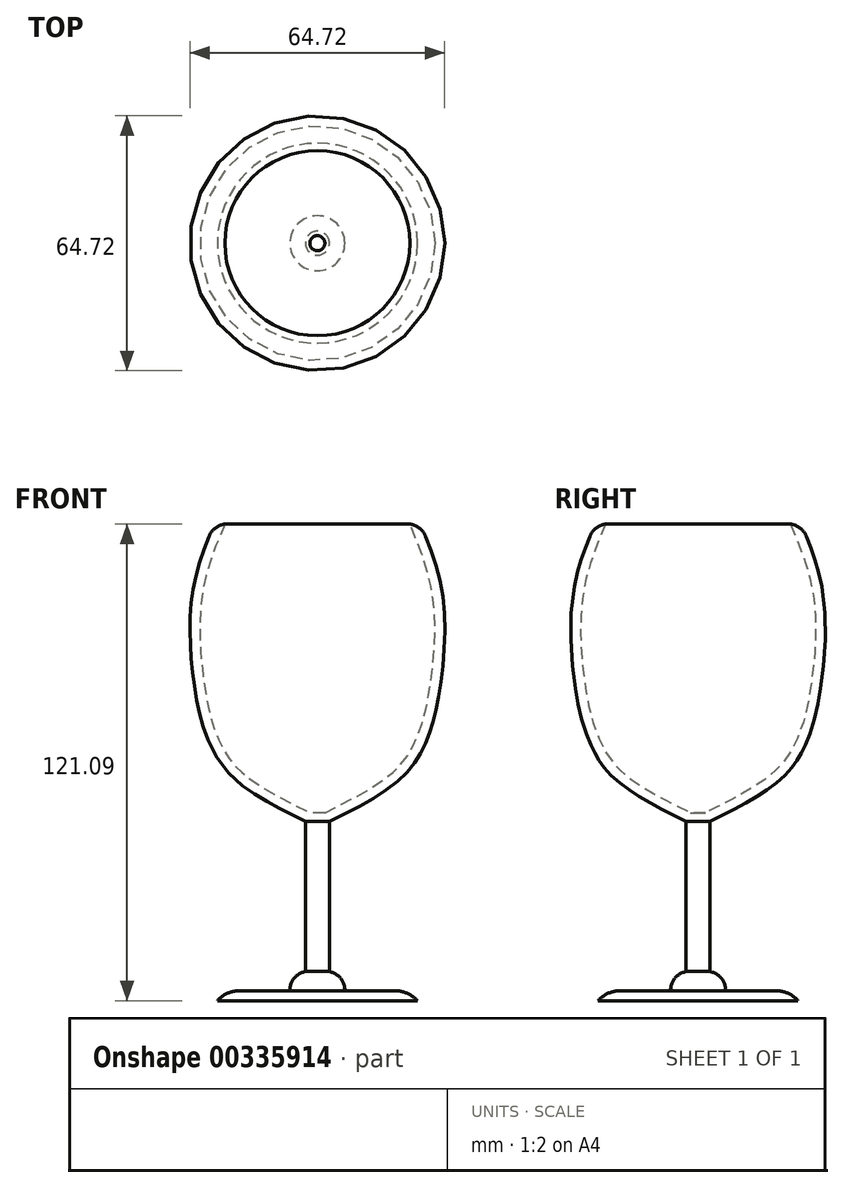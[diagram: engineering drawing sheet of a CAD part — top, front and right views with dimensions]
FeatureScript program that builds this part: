
annotation { "Feature Type Name" : "Feature", "Feature Type Description" : "" }
export const myFeature = defineFeature(function(context is Context, id is Id, definition is map)
    precondition{}
    {
        {
            var Q0;
            Q0=qCreatedBy(makeId("Front.planeOp"),FACE);
            var sketch = newSketch(context, id + "F0", { "sketchPlane" : qUnion([Q0])});
            skLineSegment(sketch, "E0", {"start": v(0, 0) * mm, "end": v(25.4, 0) * mm});
            skLineSegment(sketch, "E1", {"start": v(25.4, 0) * mm, "end": v(25.4, 2.54) * mm});
            skLineSegment(sketch, "E2", {"start": v(25.4, 2.54) * mm, "end": v(6.99, 2.54) * mm});
            skLineSegment(sketch, "E3", {"start": v(6.99, 2.54) * mm, "end": v(6.99, 7.38) * mm});
            skLineSegment(sketch, "E4", {"start": v(6.99, 7.38) * mm, "end": v(3.05, 7.38) * mm});
            skLineSegment(sketch, "E5", {"start": v(3.05, 7.38) * mm, "end": v(3.05, 45.48) * mm});
            skFitSpline(sketch, "E6", {"points": [v(3.05, 45.48) * mm, v(21.02, 56.27) * mm, v(27.66, 65.93) * mm, v(30.98, 78.3) * mm, v(31.88, 102.45) * mm, v(25.85, 122.06) * mm], "startDerivative": vector(93.63, 47.05) * mm, "endDerivative": vector(-35.34, 85.66) * mm});
            skFitSpline(sketch, "E7.0", {"points": [v(1.91, 47.75) * mm, v(3.86, 48.73) * mm, v(7.74, 50.68) * mm, v(12.23, 53.14) * mm, v(15.42, 55.15) * mm, v(17.21, 56.41) * mm, v(18.5, 57.44) * mm, v(19.38, 58.2) * mm, v(20.2, 58.98) * mm, v(21.18, 60.03) * mm, v(22.28, 61.37) * mm, v(23.4, 63.04) * mm, v(24.35, 64.77) * mm, v(25.05, 66.27) * mm, v(25.57, 67.51) * mm, v(26.05, 68.76) * mm, v(26.82, 71) * mm, v(27.56, 73.81) * mm, v(28.12, 76.63) * mm, v(28.42, 78.37) * mm, v(28.71, 80.2) * mm, v(29.05, 82.62) * mm, v(29.51, 86.74) * mm, v(29.8, 91.1) * mm, v(29.84, 95.48) * mm, v(29.72, 98.7) * mm, v(29.48, 101.3) * mm, v(29.2, 103.3) * mm, v(28.86, 105.25) * mm, v(28.33, 107.63) * mm, v(27.29, 111.32) * mm, v(25.7, 115.78) * mm, v(24.24, 119.3) * mm, v(23.5, 121.1) * mm]});
            skLineSegment(sketch, "E8", {"start": v(23.5, 121.1) * mm, "end": v(25.85, 122.06) * mm});
            skLineSegment(sketch, "E9", {"start": v(1.91, 47.75) * mm, "end": v(0, 47.75) * mm});
            skLineSegment(sketch, "E10", {"start": v(0, 47.75) * mm, "end": v(0, 0) * mm});
            skSolve(sketch);
        }
        {
            var Q0;
            Q0=makeQuery(id+"F0.imprint","IMPRINT",FACE,{"disambiguationData":[TD([[makeQuery(id+"F0.imprint","IMPRINT",EDGE,{"derivedFrom":sQuery(id+"F0.wireOp",EDGE,"E0")}),1.0]])]});
            var Q1;
            Q1=sQuery(id+"F0.wireOp",EDGE,"E10");
            revolve(context, id + "F1", {"entities" : qUnion([Q0]), "axis" : qUnion([Q1]), "revolveType" : RevolveType.FULL});
        }
        {
            var Q0;
            Q0=makeQuery(id+"F1.opRevolve","SWEPT_EDGE",EDGE,{"disambiguationData":[OSD([sQuery(id+"F0.wireOp",EDGE,"E3"),sQuery(id+"F0.wireOp",EDGE,"E4")])]});
            fillet(context, id + "F2", {"entities" : qUnion([Q0]), "radius" : 4.83 * mm, "tangentPropagation" : true, "allowEdgeOverflow" : false});
        }
        {
            var Q0;
            Q0=makeQuery(id+"F1.opRevolve","SWEPT_EDGE",EDGE,{"disambiguationData":[OSD([sQuery(id+"F0.wireOp",EDGE,"E1"),sQuery(id+"F0.wireOp",EDGE,"E2")])]});
            fillet(context, id + "F3", {"entities" : qUnion([Q0]), "radius" : 7.62 * mm, "tangentPropagation" : true, "allowEdgeOverflow" : false});
        }
        {
            var Q0;
            Q0=makeQuery(id+"F1.opRevolve","SWEPT_EDGE",EDGE,{"disambiguationData":[OSD([sQuery(id+"F0.wireOp",EDGE,"E6"),sQuery(id+"F0.wireOp",EDGE,"E8")])]});
            fillet(context, id + "F4", {"entities" : qUnion([Q0]), "radius" : 5.08 * mm, "tangentPropagation" : true, "allowEdgeOverflow" : false});
        }
    });
